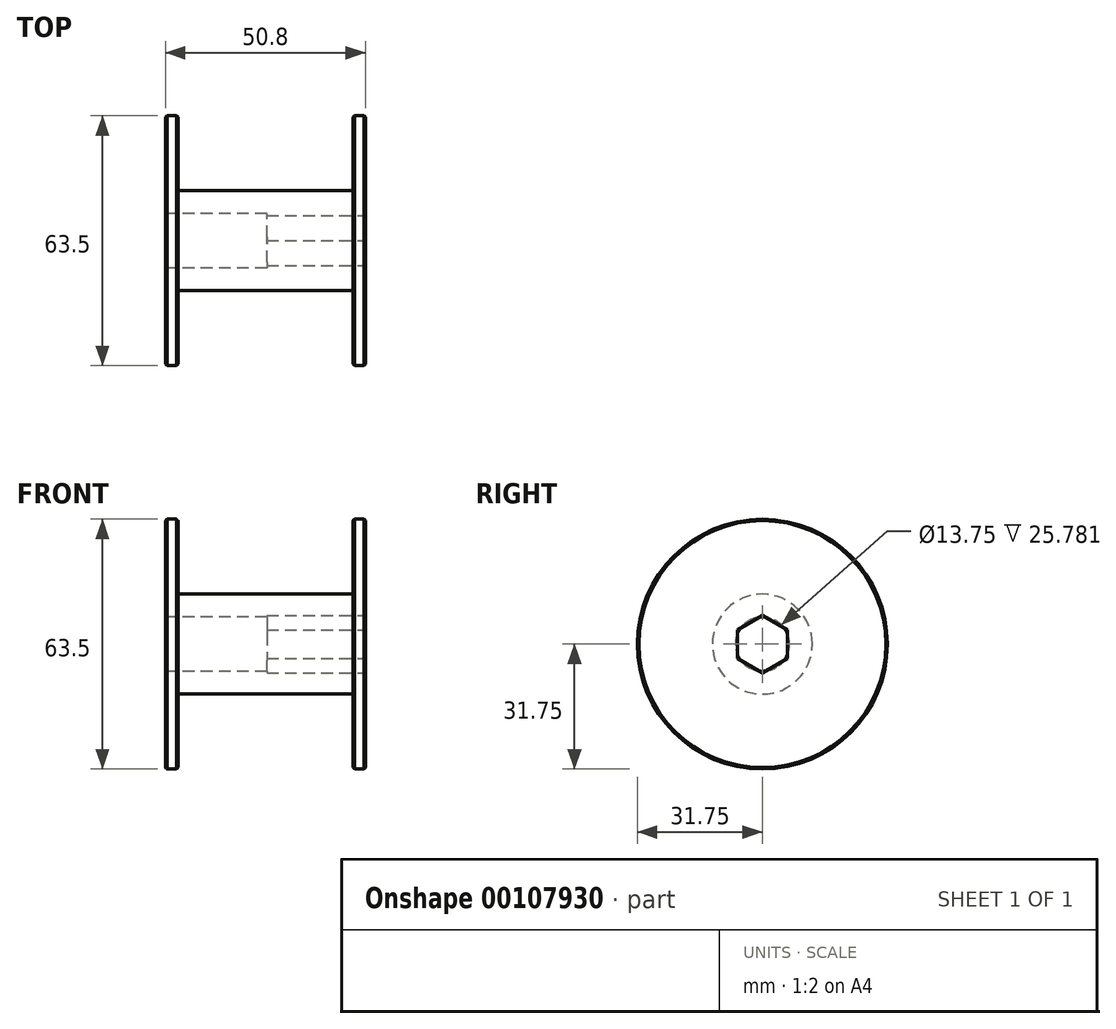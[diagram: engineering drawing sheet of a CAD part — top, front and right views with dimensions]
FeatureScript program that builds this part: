
annotation { "Feature Type Name" : "Feature", "Feature Type Description" : "" }
export const myFeature = defineFeature(function(context is Context, id is Id, definition is map)
    precondition{}
    {
        {
            var Q0;
            Q0=qCreatedBy(makeId("Front.planeOp"),FACE);
            var sketch = newSketch(context, id + "F0", { "sketchPlane" : qUnion([Q0])});
            skLineSegment(sketch, "E0", {"start": v(-22.23, 12.7) * mm, "end": v(22.23, 12.7) * mm});
            skLineSegment(sketch, "E1", {"start": v(22.23, 12.7) * mm, "end": v(22.23, 31.75) * mm});
            skLineSegment(sketch, "E2", {"start": v(22.23, 31.75) * mm, "end": v(25.4, 31.75) * mm});
            skLineSegment(sketch, "E3", {"start": v(25.4, 31.75) * mm, "end": v(25.4, 0) * mm});
            skLineSegment(sketch, "E4", {"start": v(-22.23, 12.7) * mm, "end": v(-22.23, 31.75) * mm});
            skLineSegment(sketch, "E5", {"start": v(-22.23, 31.75) * mm, "end": v(-25.4, 31.75) * mm});
            skLineSegment(sketch, "E6", {"start": v(-25.4, 31.75) * mm, "end": v(-25.4, 0) * mm});
            skLineSegment(sketch, "E7", {"start": v(-25.4, 0) * mm, "end": v(25.4, 0) * mm});
            skSolve(sketch);
        }
        {
            var Q0;
            Q0=makeQuery(id+"F0.imprint","IMPRINT",FACE,{"disambiguationData":[TD([[makeQuery(id+"F0.imprint","IMPRINT",EDGE,{"derivedFrom":sQuery(id+"F0.wireOp",EDGE,"E0")}),-1.0]])]});
            var Q1;
            Q1=sQuery(id+"F0.wireOp",EDGE,"E7");
            revolve(context, id + "F1", {"entities" : qUnion([Q0]), "axis" : qUnion([Q1]), "revolveType" : RevolveType.FULL});
        }
        {
            var Q0;
            Q0=makeQuery(id+"F1.opRevolve","SWEPT_EDGE",EDGE,{"disambiguationData":[OSD([sQuery(id+"F0.wireOp",EDGE,"E4"),sQuery(id+"F0.wireOp",EDGE,"E5")])]});
            var Q1;
            Q1=makeQuery(id+"F1.opRevolve","SWEPT_EDGE",EDGE,{"disambiguationData":[OSD([sQuery(id+"F0.wireOp",EDGE,"E5"),sQuery(id+"F0.wireOp",EDGE,"E6")])]});
            var Q2;
            Q2=makeQuery(id+"F1.opRevolve","SWEPT_EDGE",EDGE,{"disambiguationData":[OSD([sQuery(id+"F0.wireOp",EDGE,"E1"),sQuery(id+"F0.wireOp",EDGE,"E2")])]});
            var Q3;
            Q3=makeQuery(id+"F1.opRevolve","SWEPT_EDGE",EDGE,{"disambiguationData":[OSD([sQuery(id+"F0.wireOp",EDGE,"E2"),sQuery(id+"F0.wireOp",EDGE,"E3")])]});
            chamfer(context, id + "F2", {"entities" : qUnion([Q0, Q1, Q2, Q3]), "width" : 0.38 * mm, "tangentPropagation" : true});
        }
        {
            var Q0;
            Q0=makeQuery(id+"F1.opRevolve","SWEPT_FACE",FACE,{"disambiguationData":[OSD([sQuery(id+"F0.wireOp",EDGE,"E3")])]});
            var sketch = newSketch(context, id + "F3", { "sketchPlane" : qUnion([Q0])});
            skCircle(sketch, "E8.cCircle", {"center": v(0, 0) * mm, "radius": 6.35 * mm, "construction": true});
            skLineSegment(sketch, "E8.0", {"start": v(6.35, 3.67) * mm, "end": v(6.35, -3.67) * mm});
            skLineSegment(sketch, "E8.1", {"start": v(6.35, -3.67) * mm, "end": v(0, -7.33) * mm});
            skLineSegment(sketch, "E8.2", {"start": v(0, -7.33) * mm, "end": v(-6.35, -3.67) * mm});
            skLineSegment(sketch, "E8.3", {"start": v(-6.35, -3.67) * mm, "end": v(-6.35, 3.67) * mm});
            skLineSegment(sketch, "E8.4", {"start": v(-6.35, 3.67) * mm, "end": v(0, 7.33) * mm});
            skLineSegment(sketch, "E8.5", {"start": v(0, 7.33) * mm, "end": v(6.35, 3.67) * mm});
            skPoint(sketch, "E8.0.midPoint", {"position": v(6.35, 0) * mm});
            skSolve(sketch);
        }
        {
            var Q0;
            Q0=makeQuery(id+"F3.imprint","IMPRINT",FACE,{"disambiguationData":[TD([[makeQuery(id+"F3.imprint","IMPRINT",EDGE,{"derivedFrom":sQuery(id+"F3.wireOp",EDGE,"E8.0")}),-1.0]])]});
            extrude(context, id + "F4", {"entities" : qUnion([Q0]), "operationType" : NewBodyOperationType.REMOVE, "oppositeDirection" : true, "depth" : 25.02 * mm});
        }
        {
            var Q0;
            Q0=makeQuery(id+"F1.opRevolve","SWEPT_FACE",FACE,{"disambiguationData":[OSD([sQuery(id+"F0.wireOp",EDGE,"E6")])]});
            var sketch = newSketch(context, id + "F5", { "sketchPlane" : qUnion([Q0])});
            skCircle(sketch, "E9", {"center": v(0, 0) * mm, "radius": 6.88 * mm});
            skSolve(sketch);
        }
        {
            var Q0;
            Q0=makeQuery(id+"F5.imprint","IMPRINT",FACE,{"disambiguationData":[TD([[makeQuery(id+"F5.imprint","IMPRINT",EDGE,{"derivedFrom":sQuery(id+"F5.wireOp",EDGE,"E9")}),1.0]])]});
            extrude(context, id + "F6", {"entities" : qUnion([Q0]), "operationType" : NewBodyOperationType.REMOVE, "oppositeDirection" : true, "depth" : 25.78 * mm});
        }
    });
